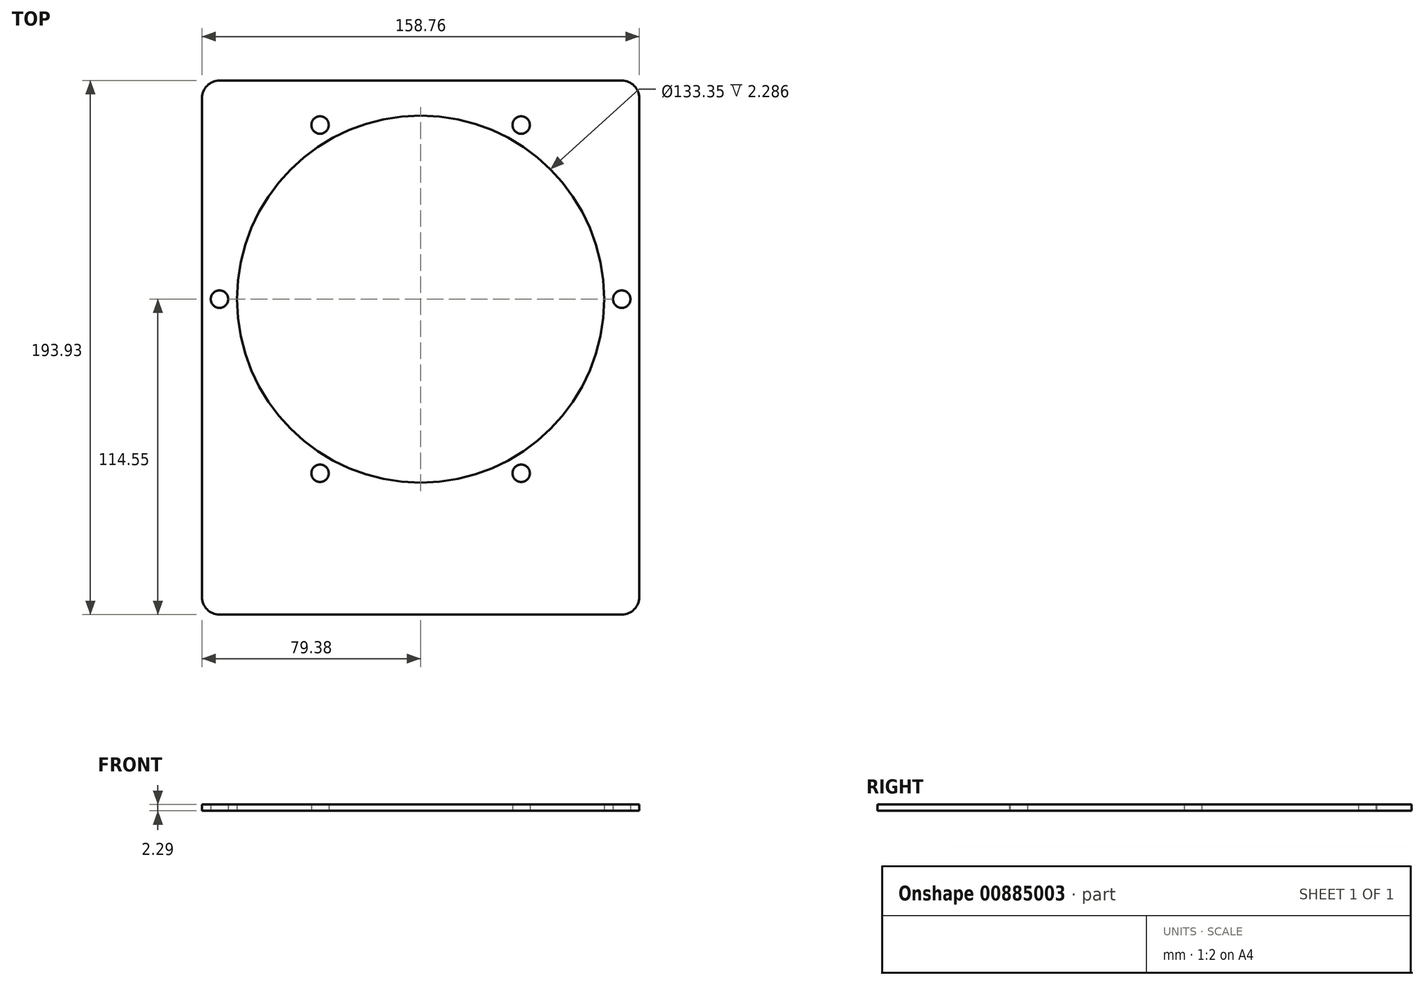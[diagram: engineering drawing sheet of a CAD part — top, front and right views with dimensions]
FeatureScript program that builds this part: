
annotation { "Feature Type Name" : "Feature", "Feature Type Description" : "" }
export const myFeature = defineFeature(function(context is Context, id is Id, definition is map)
    precondition{}
    {
        {
            var Q0;
            Q0=qCreatedBy(makeId("Top.planeOp"),FACE);
            var sketch = newSketch(context, id + "F0", { "sketchPlane" : qUnion([Q0])});
            skCircle(sketch, "E0", {"center": v(0, 0) * mm, "radius": 66.68 * mm});
            skLineSegment(sketch, "E1.bottom", {"start": v(-73.03, 79.38) * mm, "end": v(73.03, 79.38) * mm});
            skLineSegment(sketch, "E1.top", {"start": v(-73.03, -114.55) * mm, "end": v(73.03, -114.55) * mm});
            skLineSegment(sketch, "E1.left", {"start": v(-79.38, 73.03) * mm, "end": v(-79.38, -108.2) * mm});
            skLineSegment(sketch, "E1.right", {"start": v(79.38, 73.03) * mm, "end": v(79.38, -108.2) * mm});
            skPoint(sketch, "E2.visualSharp", {"position": v(-79.38, 79.38) * mm});
            skArc(sketch, "E2.filletArc", {"start": v(-73.03, 79.38) * mm, "mid": v(-77.52, 77.52) * mm, "end": v(-79.38, 73.03) * mm});
            skPoint(sketch, "E3.visualSharp", {"position": v(-79.37, -114.55) * mm});
            skArc(sketch, "E3.filletArc", {"start": v(-79.38, -108.2) * mm, "mid": v(-77.52, -112.7) * mm, "end": v(-73.03, -114.55) * mm});
            skPoint(sketch, "E4.visualSharp", {"position": v(79.38, -114.55) * mm});
            skArc(sketch, "E4.filletArc", {"start": v(73.03, -114.55) * mm, "mid": v(77.52, -112.7) * mm, "end": v(79.38, -108.2) * mm});
            skPoint(sketch, "E5.visualSharp", {"position": v(79.38, 79.38) * mm});
            skArc(sketch, "E5.filletArc", {"start": v(79.38, 73.03) * mm, "mid": v(77.52, 77.52) * mm, "end": v(73.03, 79.38) * mm});
            skSolve(sketch);
        }
        {
            var Q0;
            Q0=makeQuery(id+"F0.imprint","IMPRINT",FACE,{"disambiguationData":[TD([[makeQuery(id+"F0.imprint","IMPRINT",EDGE,{"derivedFrom":sQuery(id+"F0.wireOp",EDGE,"E0")}),-1.0]])]});
            var Q1;
            Q1=makeQuery(id+"F0.imprint","IMPRINT",FACE,{"disambiguationData":[TD([[makeQuery(id+"F0.imprint","IMPRINT",EDGE,{"derivedFrom":sQuery(id+"F0.wireOp",EDGE,"E1.bottom")}),-1.0]])]});
            extrude(context, id + "F1", {"entities" : qUnion([Q0, Q1]), "depth" : 2.3 * mm, "offsetDistance" : 25.4 * mm});
        }
        {
            var Q0;
            Q0=makeQuery(id+"F0.imprint","IMPRINT",FACE,{"disambiguationData":[TD([[makeQuery(id+"F0.imprint","IMPRINT",EDGE,{"derivedFrom":sQuery(id+"F0.wireOp",EDGE,"E1.bottom")}),-1.0]])]});
            var sketch = newSketch(context, id + "F2", { "sketchPlane" : qUnion([Q0])});
            skCircle(sketch, "E6", {"center": v(-73.03, 0) * mm, "radius": 3.18 * mm});
            skCircle(sketch, "E7.1.0", {"center": v(-36.51, -63.24) * mm, "radius": 3.18 * mm});
            skCircle(sketch, "E7.2.0", {"center": v(36.51, -63.24) * mm, "radius": 3.18 * mm});
            skPoint(sketch, "E7.center", {"position": v(0, 0) * mm});
            skCircle(sketch, "E8.1.3.0", {"center": v(73.03, 0) * mm, "radius": 3.18 * mm});
            skCircle(sketch, "E8.1.4.0", {"center": v(36.51, 63.24) * mm, "radius": 3.18 * mm});
            skCircle(sketch, "E8.1.5.0", {"center": v(-36.51, 63.24) * mm, "radius": 3.18 * mm});
            skSolve(sketch);
        }
        {
            var Q0;
            Q0 = qSketchRegion(id + "F2", true);
            extrude(context, id + "F3", {"entities" : qUnion([Q0]), "operationType" : NewBodyOperationType.REMOVE, "depth" : 25.4 * mm, "offsetDistance" : 25.4 * mm});
        }
    });
